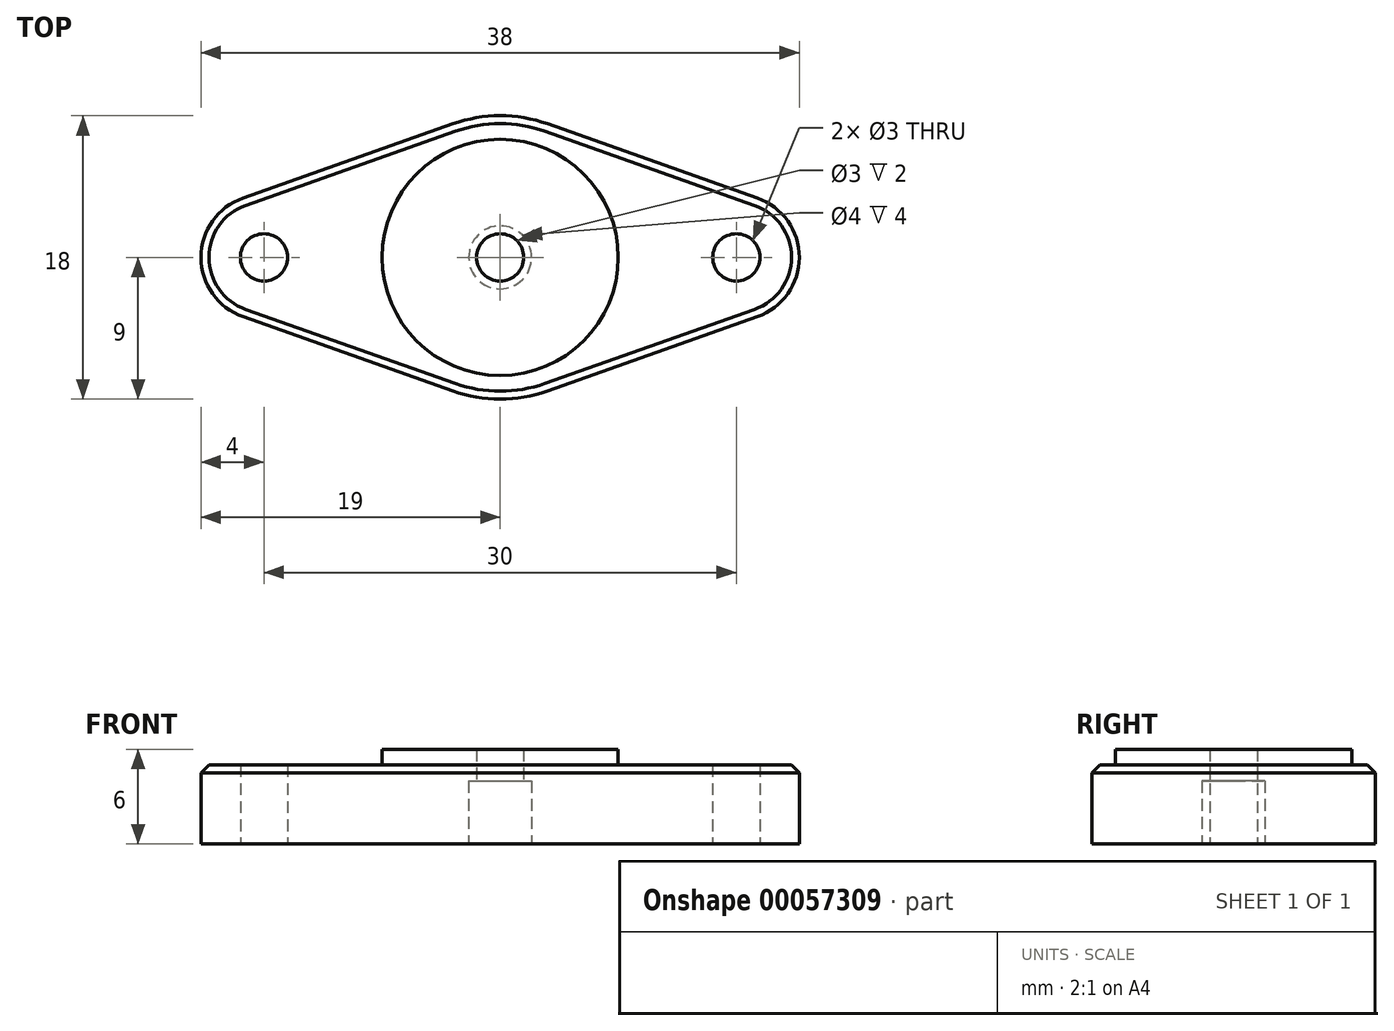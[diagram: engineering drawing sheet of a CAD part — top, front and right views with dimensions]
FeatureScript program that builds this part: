
annotation { "Feature Type Name" : "Feature", "Feature Type Description" : "" }
export const myFeature = defineFeature(function(context is Context, id is Id, definition is map)
    precondition{}
    {
        {
            var Q0;
            Q0=qCreatedBy(makeId("Top.planeOp"),FACE);
            var sketch = newSketch(context, id + "F0", { "sketchPlane" : qUnion([Q0])});
            skCircle(sketch, "E0", {"center": v(0, 0) * mm, "radius": 9 * mm, "construction": true});
            skCircle(sketch, "E1", {"center": v(15, 0) * mm, "radius": 1.5 * mm});
            skCircle(sketch, "E2", {"center": v(15, 0) * mm, "radius": 4 * mm, "construction": true});
            skCircle(sketch, "E3", {"center": v(-15, 0) * mm, "radius": 1.5 * mm});
            skCircle(sketch, "E4", {"center": v(-15, 0) * mm, "radius": 4 * mm, "construction": true});
            skLineSegment(sketch, "E5", {"start": v(0, 0) * mm, "end": v(0, 9) * mm, "construction": true});
            skLineSegment(sketch, "E6", {"start": v(-15, 0) * mm, "end": v(15, 0) * mm, "construction": true});
            skLineSegment(sketch, "E7", {"start": v(0, 0) * mm, "end": v(0, -9) * mm, "construction": true});
            skLineSegment(sketch, "E8", {"start": v(-15, 0) * mm, "end": v(-15, 4) * mm, "construction": true});
            skLineSegment(sketch, "E9", {"start": v(15, 0) * mm, "end": v(15, 4) * mm, "construction": true});
            skLineSegment(sketch, "E10", {"start": v(-16.33, 3.77) * mm, "end": v(-3, 8.49) * mm});
            skLineSegment(sketch, "E11", {"start": v(-16.33, -3.77) * mm, "end": v(-3, -8.49) * mm});
            skLineSegment(sketch, "E12", {"start": v(3, -8.49) * mm, "end": v(16.33, -3.77) * mm});
            skLineSegment(sketch, "E13", {"start": v(16.33, 3.77) * mm, "end": v(3, 8.49) * mm});
            skArc(sketch, "E14", {"start": v(-16.33, -3.77) * mm, "mid": v(-19, 0) * mm, "end": v(-16.33, 3.77) * mm});
            skArc(sketch, "E15", {"start": v(16.33, -3.77) * mm, "mid": v(19, 0) * mm, "end": v(16.33, 3.77) * mm});
            skCircle(sketch, "E16", {"center": v(0, 0) * mm, "radius": 6 * mm, "construction": true});
            skArc(sketch, "E17", {"start": v(-3, 8.49) * mm, "mid": v(0, 9) * mm, "end": v(3, 8.49) * mm});
            skArc(sketch, "E18", {"start": v(-3, -8.49) * mm, "mid": v(0, -9) * mm, "end": v(3, -8.49) * mm});
            skSolve(sketch);
        }
        {
            var Q0;
            Q0 = qSketchRegion(id + "F0", true);
            extrude(context, id + "F1", {"entities" : qUnion([Q0]), "depth" : 5 * mm});
        }
        {
            var Q0;
            Q0=makeQuery(id+"F1.opExtrude","CAP_FACE",FACE,{"disambiguationData":[OSD([sQuery(id+"F0.wireOp",EDGE,"E1"),sQuery(id+"F0.wireOp",EDGE,"E3"),sQuery(id+"F0.wireOp",EDGE,"E10"),sQuery(id+"F0.wireOp",EDGE,"E11"),sQuery(id+"F0.wireOp",EDGE,"E12"),sQuery(id+"F0.wireOp",EDGE,"E13"),sQuery(id+"F0.wireOp",EDGE,"E14"),sQuery(id+"F0.wireOp",EDGE,"E15"),sQuery(id+"F0.wireOp",EDGE,"E17"),sQuery(id+"F0.wireOp",EDGE,"E18")])],"isStart":true});
            var sketch = newSketch(context, id + "F2", { "sketchPlane" : qUnion([Q0])});
            skLineSegment(sketch, "E19", {"start": v(15, 0) * mm, "end": v(-15, 0) * mm, "construction": true});
            skLineSegment(sketch, "E20", {"start": v(0, 9) * mm, "end": v(0, -9) * mm, "construction": true});
            skPoint(sketch, "E21", {"position": v(0, 0) * mm});
            skCircle(sketch, "E22", {"center": v(0, 0) * mm, "radius": 1.5 * mm});
            skSolve(sketch);
        }
        {
            var Q0;
            Q0 = qSketchRegion(id + "F2", true);
            extrude(context, id + "F3", {"entities" : qUnion([Q0]), "operationType" : NewBodyOperationType.REMOVE, "endBound" : BoundingType.THROUGH_ALL, "oppositeDirection" : true, "depth" : 25 * mm});
        }
        {
            var Q0;
            Q0=makeQuery(id+"F1.opExtrude","CAP_FACE",FACE,{"disambiguationData":[OSD([sQuery(id+"F0.wireOp",EDGE,"E1"),sQuery(id+"F0.wireOp",EDGE,"E3"),sQuery(id+"F0.wireOp",EDGE,"E10"),sQuery(id+"F0.wireOp",EDGE,"E11"),sQuery(id+"F0.wireOp",EDGE,"E12"),sQuery(id+"F0.wireOp",EDGE,"E13"),sQuery(id+"F0.wireOp",EDGE,"E14"),sQuery(id+"F0.wireOp",EDGE,"E15"),sQuery(id+"F0.wireOp",EDGE,"E17"),sQuery(id+"F0.wireOp",EDGE,"E18")])],"isStart":true});
            var sketch = newSketch(context, id + "F4", { "sketchPlane" : qUnion([Q0])});
            skLineSegment(sketch, "E23", {"start": v(-15, 0) * mm, "end": v(15, 0) * mm, "construction": true});
            skCircle(sketch, "E24", {"center": v(0, 0) * mm, "radius": 2 * mm});
            skSolve(sketch);
        }
        {
            var Q0;
            Q0 = qSketchRegion(id + "F4", true);
            extrude(context, id + "F5", {"entities" : qUnion([Q0]), "operationType" : NewBodyOperationType.REMOVE, "oppositeDirection" : true, "depth" : 4 * mm});
        }
        {
            var Q0;
            Q0=makeQuery(id+"F1.opExtrude","CAP_FACE",FACE,{"disambiguationData":[OSD([sQuery(id+"F0.wireOp",EDGE,"E1"),sQuery(id+"F0.wireOp",EDGE,"E3"),sQuery(id+"F0.wireOp",EDGE,"E10"),sQuery(id+"F0.wireOp",EDGE,"E11"),sQuery(id+"F0.wireOp",EDGE,"E12"),sQuery(id+"F0.wireOp",EDGE,"E13"),sQuery(id+"F0.wireOp",EDGE,"E14"),sQuery(id+"F0.wireOp",EDGE,"E15"),sQuery(id+"F0.wireOp",EDGE,"E17"),sQuery(id+"F0.wireOp",EDGE,"E18")])],"isStart":false});
            var sketch = newSketch(context, id + "F6", { "sketchPlane" : qUnion([Q0])});
            skCircle(sketch, "E25", {"center": v(0, 0) * mm, "radius": 7.5 * mm});
            skCircle(sketch, "E26", {"center": v(0, 0) * mm, "radius": 1.5 * mm});
            skSolve(sketch);
        }
        {
            var Q0;
            Q0 = qSketchRegion(id + "F6", true);
            extrude(context, id + "F7", {"entities" : qUnion([Q0]), "operationType" : NewBodyOperationType.ADD, "depth" : 1 * mm});
        }
        {
            var Q0;
            Q0=makeQuery(id+"F1.opExtrude","CAP_EDGE",EDGE,{"disambiguationData":[OSD([sQuery(id+"F0.wireOp",EDGE,"E13")])],"isStart":false});
            chamfer(context, id + "F8", {"entities" : qUnion([Q0]), "width" : 0.5 * mm, "tangentPropagation" : true});
        }
    });
